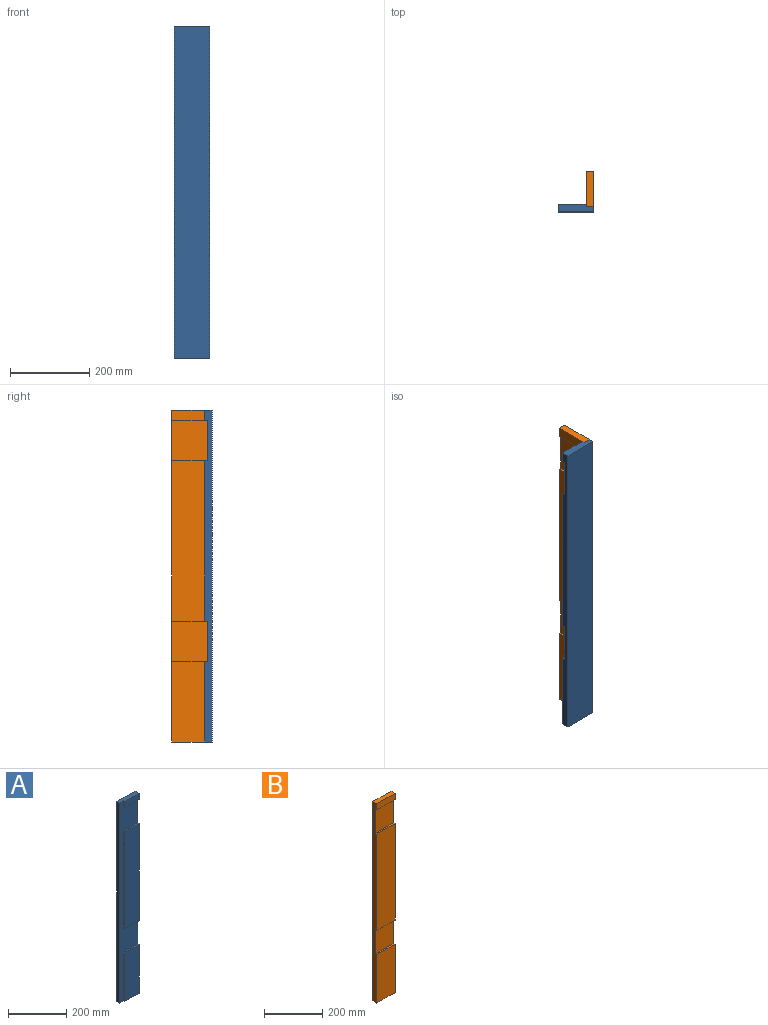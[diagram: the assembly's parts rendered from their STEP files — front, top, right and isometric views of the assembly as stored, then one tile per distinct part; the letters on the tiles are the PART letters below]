
ASSEMBLY  parts=2 mates=1
PART A: 16 faces, bbox 88.9x19.1x838.2 mm
  f0: plane 69.85x25.4mm, normal (0,-1,0), area 1774.2mm2, adj f4,f7,f11,f14
  f1: plane 203.2x69.85mm, normal (0,-1,0), area 14193.5mm2, adj f3,f4,f8,f13
  f2: plane 406.4x6.35mm, normal (-1,0,0), area 2580.6mm2, adj f6,f10,f12,f15
  f3: plane 203.2x6.35mm, normal (-1,0,0), area 1290.3mm2, adj f1,f8,f10,f13
  f4: plane 838.2x19.05mm, normal (1,0,0), area 14677.4mm2, adj f0,f1,f6,f7,f8,f9,f10,f12
  f5: plane 838.2x12.7mm, normal (-1,0,0), area 10645.1mm2, adj f7,f8,f9,f10
  f6: plane 406.4x69.85mm, normal (0,-1,0), area 28387mm2, adj f2,f4,f12,f15
  f7: plane 88.9x19.05mm, normal (0,0,1), area 1572.6mm2, adj f0,f4,f5,f9,f10,f11
  f8: plane 88.9x19.05mm, normal (0,0,-1), area 1572.6mm2, adj f1,f3,f4,f5,f9,f10
  f9: plane 838.2x88.9mm, normal (0,1,0), area 74516mm2, adj f4,f5,f7,f8
  f10: plane 838.2x88.9mm, normal (0,-1,0), area 30161.2mm2, adj f2,f3,f4,f5,f7,f8,f11,f12
  f11: plane 25.4x6.35mm, normal (-1,0,0), area 161.3mm2, adj f0,f7,f10,f14
  f12: plane 69.85x6.35mm, normal (0,0,-1), area 443.5mm2, adj f2,f4,f6,f10
  f13: plane 69.85x6.35mm, normal (0,0,1), area 443.5mm2, adj f1,f3,f4,f10
  f14: plane 69.85x6.35mm, normal (0,0,-1), area 443.5mm2, adj f0,f4,f10,f11
  f15: plane 69.85x6.35mm, normal (0,0,1), area 443.5mm2, adj f2,f4,f6,f10
PART B: 14 faces, bbox 88.9x19.1x838.2 mm
  f0: plane 406.4x88.9mm, normal (0,-1,0), area 36129mm2, adj f2,f3,f8,f12
  f1: plane 203.2x88.9mm, normal (0,-1,0), area 18064.5mm2, adj f2,f3,f6,f9
  f2: plane 838.2x19.05mm, normal (-1,0,0), area 14677.4mm2, adj f0,f1,f4,f5,f6,f7,f8,f9
  f3: plane 838.2x19.05mm, normal (1,0,0), area 14677.4mm2, adj f0,f1,f4,f5,f6,f7,f8,f9
  f4: plane 838.2x88.9mm, normal (0,1,0), area 74516mm2, adj f2,f3,f6,f7
  f5: plane 88.9x25.4mm, normal (0,-1,0), area 2258.1mm2, adj f2,f3,f7,f11
  f6: plane 88.9x19.05mm, normal (0,0,-1), area 1693.5mm2, adj f1,f2,f3,f4
  f7: plane 88.9x19.05mm, normal (0,0,1), area 1693.5mm2, adj f2,f3,f4,f5
  f8: plane 88.9x6.35mm, normal (0,0,-1), area 564.5mm2, adj f0,f2,f3,f10
  f9: plane 88.9x6.35mm, normal (0,0,1), area 564.5mm2, adj f1,f2,f3,f10
  f10: plane 101.6x88.9mm, normal (0,-1,0), area 9032.2mm2, adj f2,f3,f8,f9
  f11: plane 88.9x6.35mm, normal (0,0,-1), area 564.5mm2, adj f2,f3,f5,f13
  f12: plane 88.9x6.35mm, normal (0,0,1), area 564.5mm2, adj f0,f2,f3,f13
  f13: plane 101.6x88.9mm, normal (0,-1,0), area 9032.2mm2, adj f2,f3,f11,f12
PLACE A rot(axis=(0,0,1),180deg) t=(78.01,-146.67,173.38)mm
PLACE B rot(axis=(0,0,-1),90deg) t=(112.93,-99.05,173.38)mm fixed
MATE fastened B.f3 <-> A.f10  axis (0,-1,0) through (122.46,-143.5,173.38)mm
